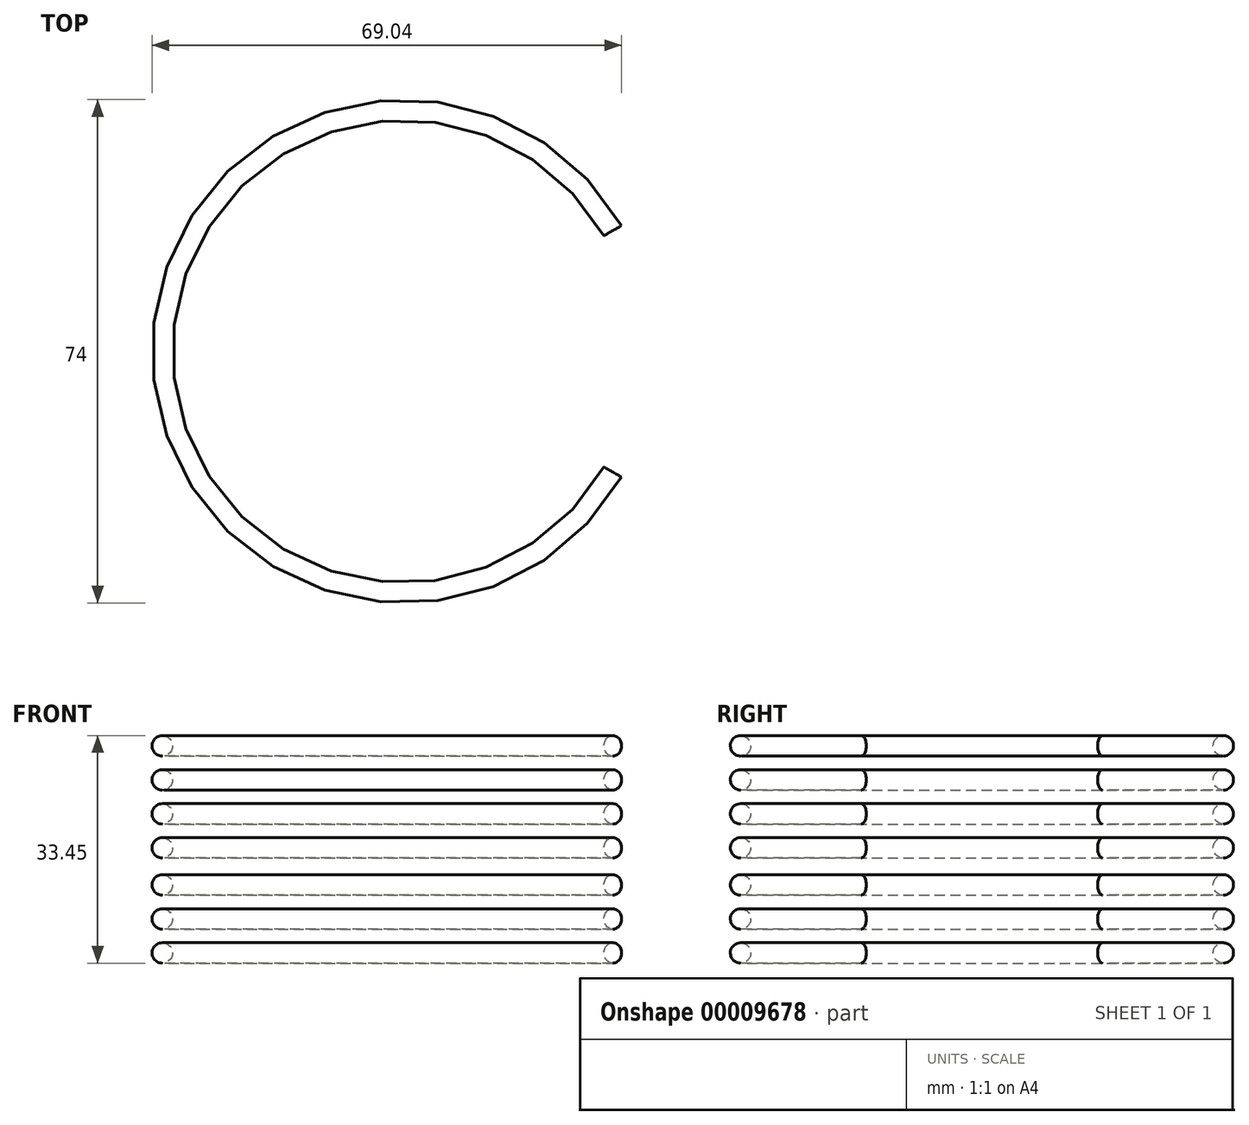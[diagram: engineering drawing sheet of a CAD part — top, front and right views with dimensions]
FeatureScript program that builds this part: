
annotation { "Feature Type Name" : "Feature", "Feature Type Description" : "" }
export const myFeature = defineFeature(function(context is Context, id is Id, definition is map)
    precondition{}
    {
        {
            var Q0;
            Q0=qCreatedBy(makeId("Front.planeOp"),FACE);
            var sketch = newSketch(context, id + "F0", { "sketchPlane" : qUnion([Q0])});
            skCircle(sketch, "E0", {"center": v(-35.5, 42) * mm, "radius": 1.5 * mm});
            skCircle(sketch, "E1", {"center": v(-35.5, 37) * mm, "radius": 1.5 * mm});
            skCircle(sketch, "E2", {"center": v(-35.5, 32) * mm, "radius": 1.5 * mm});
            skCircle(sketch, "E3", {"center": v(-35.5, 27) * mm, "radius": 1.5 * mm});
            skLineSegment(sketch, "E4", {"start": v(0, 0) * mm, "end": v(0, 30.92) * mm});
            skCircle(sketch, "E5", {"center": v(-35.5, 11.55) * mm, "radius": 1.5 * mm});
            skCircle(sketch, "E6", {"center": v(-35.5, 16.55) * mm, "radius": 1.5 * mm});
            skCircle(sketch, "E7", {"center": v(-35.5, 21.55) * mm, "radius": 1.5 * mm});
            skSolve(sketch);
        }
        {
            var Q0;
            Q0 = qSketchRegion(id + "F0", true);
            var Q1;
            Q1=sQuery(id+"F0.wireOp",EDGE,"E4");
            revolve(context, id + "F1", {"entities" : qUnion([Q0]), "axis" : qUnion([Q1]), "revolveType" : RevolveType.SYMMETRIC, "angle" : 300 * degree});
        }
    });
